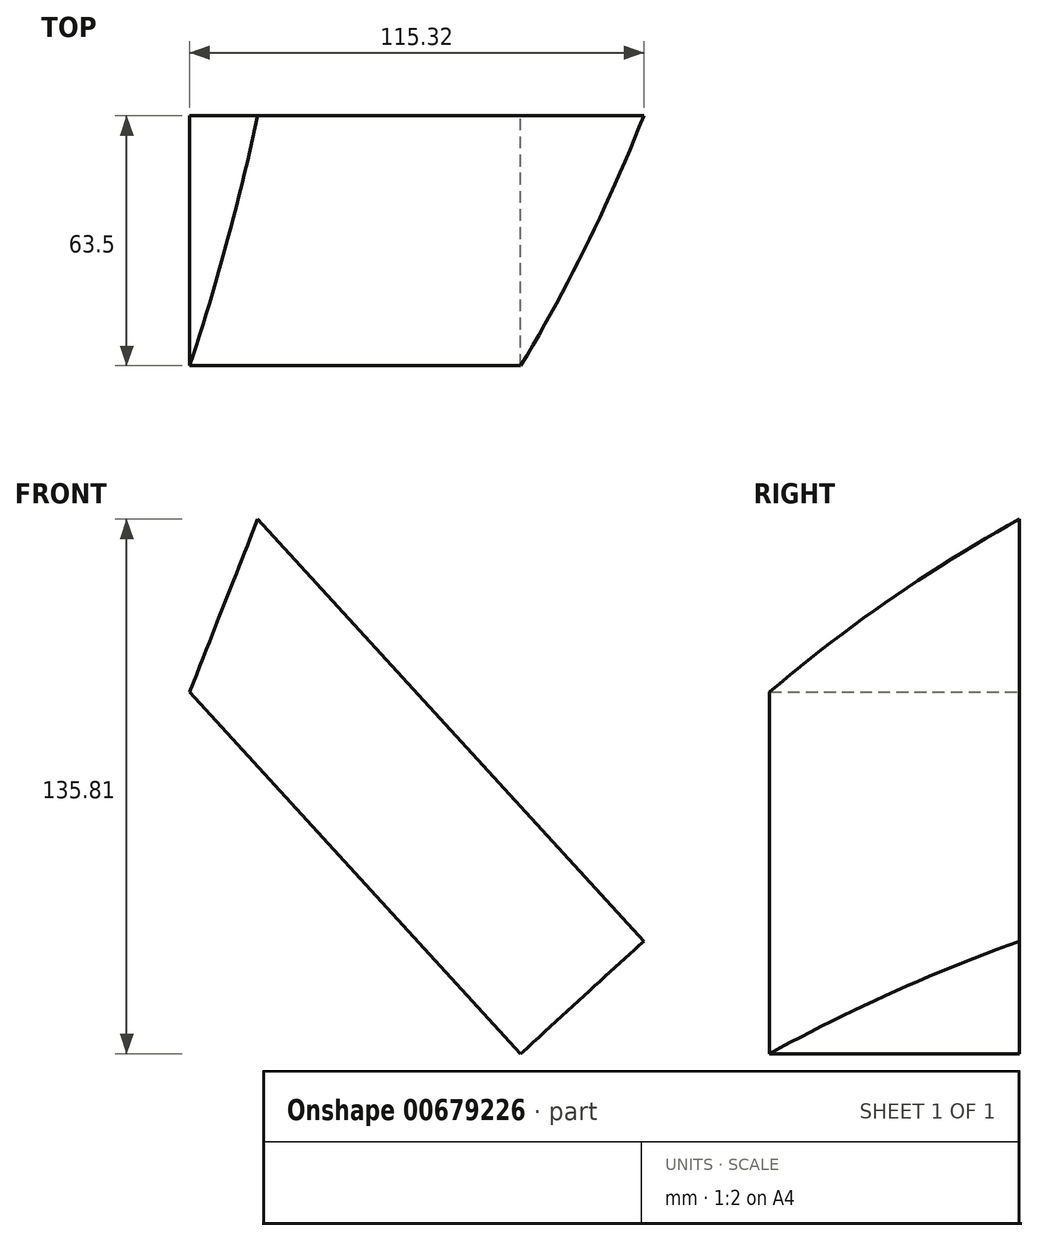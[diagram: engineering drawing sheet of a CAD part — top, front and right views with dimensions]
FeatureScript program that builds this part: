
annotation { "Feature Type Name" : "Feature", "Feature Type Description" : "" }
export const myFeature = defineFeature(function(context is Context, id is Id, definition is map)
    precondition{}
    {
        {
            var Q0;
            Q0=qCreatedBy(makeId("Front.planeOp"),FACE);
            var sketch = newSketch(context, id + "F0", { "sketchPlane" : qUnion([Q0])});
            skLineSegment(sketch, "E0", {"start": v(-95.01, 28.2) * mm, "end": v(-113.11, -17.75) * mm});
            skLineSegment(sketch, "E1", {"start": v(-113.11, -17.75) * mm, "end": v(-29.04, -109.7) * mm});
            skLineSegment(sketch, "E2", {"start": v(-29.04, -109.7) * mm, "end": v(36.02, -50.2) * mm});
            skLineSegment(sketch, "E3", {"start": v(36.02, -50.2) * mm, "end": v(-46.63, 40.2) * mm});
            skLineSegment(sketch, "E4", {"start": v(-46.63, 40.2) * mm, "end": v(-95.01, 28.2) * mm});
            skSolve(sketch);
        }
        {
            var Q0;
            Q0=makeQuery(id+"F0.imprint","IMPRINT",FACE,{"disambiguationData":[TD([[makeQuery(id+"F0.imprint","IMPRINT",EDGE,{"derivedFrom":sQuery(id+"F0.wireOp",EDGE,"E0")}),1.0]])]});
            extrude(context, id + "F1", {"entities" : qUnion([Q0]), "depth" : 63.5 * mm, "offsetDistance" : 25.4 * mm});
        }
        {
            var Q0;
            Q0=makeQuery(id+"F1.opExtrude","CAP_EDGE",EDGE,{"disambiguationData":[OSD([sQuery(id+"F0.wireOp",EDGE,"E3")])],"isStart":false});
            fillet(context, id + "F2", {"entities" : qUnion([Q0]), "radius" : 389.4 * mm, "tangentPropagation" : true, "allowEdgeOverflow" : false});
        }
    });
